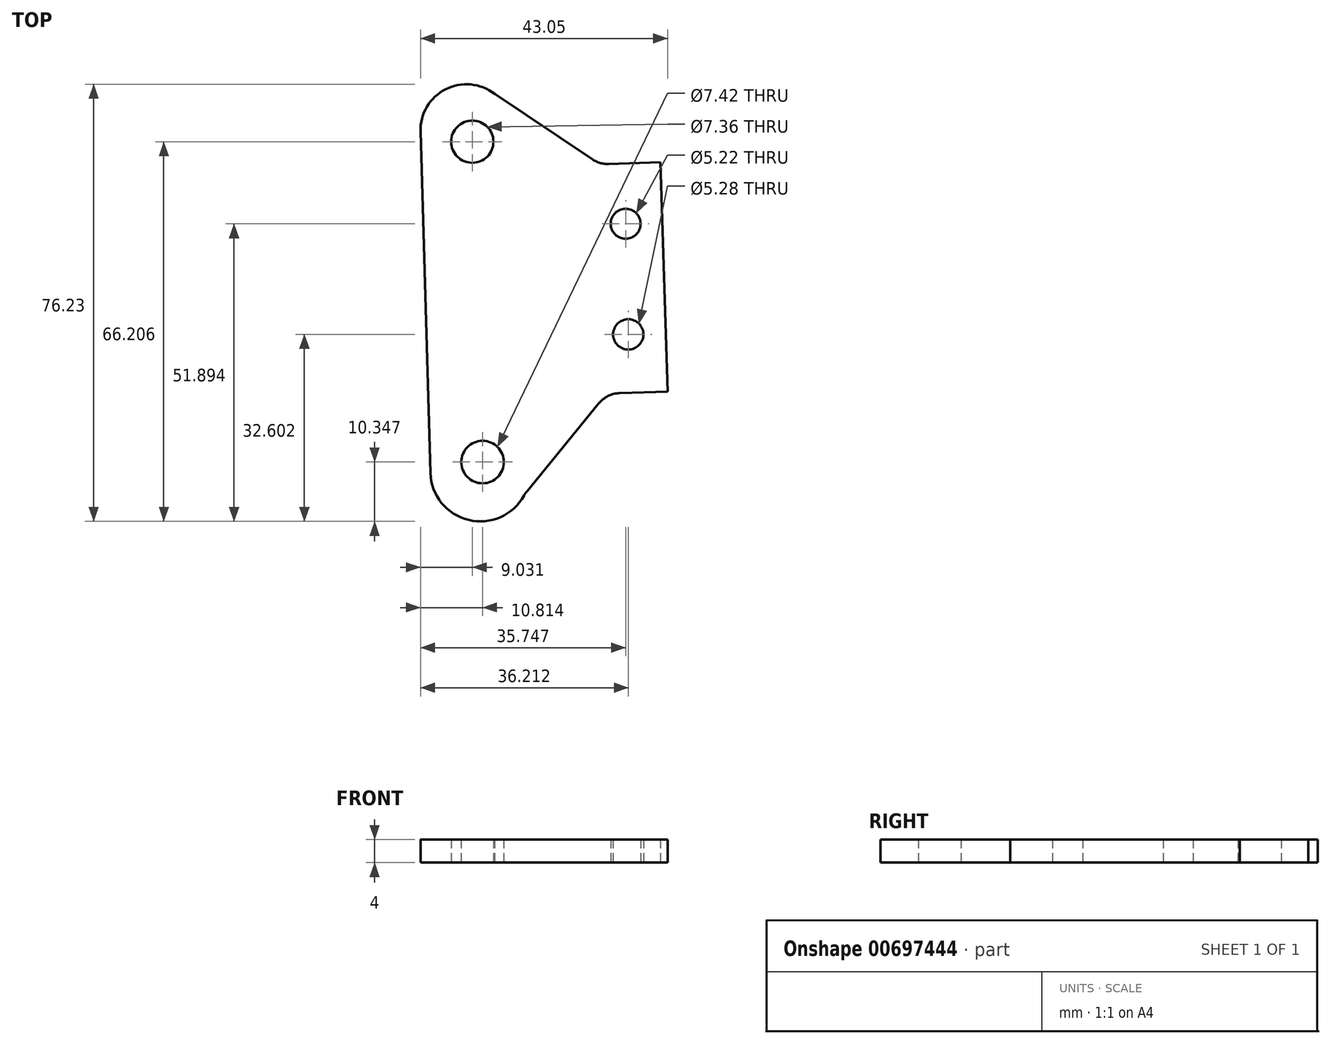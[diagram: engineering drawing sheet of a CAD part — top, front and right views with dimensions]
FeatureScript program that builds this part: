
annotation { "Feature Type Name" : "Feature", "Feature Type Description" : "" }
export const myFeature = defineFeature(function(context is Context, id is Id, definition is map)
    precondition{}
    {
        {
            var Q0;
            Q0=qCreatedBy(makeId("Top.planeOp"),FACE);
            var sketch = newSketch(context, id + "F0", { "sketchPlane" : qUnion([Q0])});
            skLineSegment(sketch, "E0", {"start": v(-13.1, -22.63) * mm, "end": v(-14.39, 17.35) * mm});
            skLineSegment(sketch, "E1", {"start": v(-13.1, -22.63) * mm, "end": v(-21.41, -22.9) * mm});
            skLineSegment(sketch, "E2", {"start": v(-14.39, 17.35) * mm, "end": v(-23.34, 17.06) * mm});
            skLineSegment(sketch, "E3", {"start": v(-56.15, 22.71) * mm, "end": v(-54.44, -36.82) * mm});
            skArc(sketch, "E4", {"start": v(-54.44, -36.82) * mm, "mid": v(-47.79, -45.02) * mm, "end": v(-38.12, -40.77) * mm});
            skArc(sketch, "E5", {"start": v(-43.27, 29.3) * mm, "mid": v(-51.8, 30.08) * mm, "end": v(-56.15, 22.71) * mm});
            skLineSegment(sketch, "E6", {"start": v(-43.27, 29.3) * mm, "end": v(-26.3, 17.9) * mm});
            skLineSegment(sketch, "E7", {"start": v(-37.62, -40.01) * mm, "end": v(-25.12, -24.73) * mm});
            skCircle(sketch, "E8", {"center": v(-45.35, -34.92) * mm, "radius": 3.7 * mm});
            skPoint(sketch, "E8.first.point", {"position": v(-49.01, -34.36) * mm});
            skPoint(sketch, "E8.second.point", {"position": v(-41.66, -35.31) * mm});
            skPoint(sketch, "E8.third.point", {"position": v(-44.89, -38.6) * mm});
            skCircle(sketch, "E9", {"center": v(-47.13, 20.94) * mm, "radius": 3.68 * mm});
            skPoint(sketch, "E9.first.point", {"position": v(-50.8, 21.12) * mm});
            skPoint(sketch, "E9.second.point", {"position": v(-43.45, 20.82) * mm});
            skPoint(sketch, "E9.third.point", {"position": v(-46.08, 17.4) * mm});
            skCircle(sketch, "E10", {"center": v(-20.41, 6.62) * mm, "radius": 2.6 * mm});
            skPoint(sketch, "E10.first.point", {"position": v(-23, 6.35) * mm});
            skPoint(sketch, "E10.second.point", {"position": v(-17.8, 6.47) * mm});
            skPoint(sketch, "E10.third.point", {"position": v(-20.26, 4.02) * mm});
            skCircle(sketch, "E11", {"center": v(-19.95, -12.67) * mm, "radius": 2.64 * mm});
            skPoint(sketch, "E11.first.point", {"position": v(-22.59, -12.72) * mm});
            skPoint(sketch, "E11.second.point", {"position": v(-17.33, -13.02) * mm});
            skPoint(sketch, "E11.third.point", {"position": v(-19.3, -15.23) * mm});
            skArc(sketch, "E12.filletArc", {"start": v(-21.41, -22.9) * mm, "mid": v(-23.47, -23.41) * mm, "end": v(-25.12, -24.73) * mm});
            skPoint(sketch, "E13.visualSharp", {"position": v(-37.94, -40.4) * mm});
            skArc(sketch, "E13.filletArc", {"start": v(-37.62, -40.01) * mm, "mid": v(-37.89, -40.38) * mm, "end": v(-38.12, -40.77) * mm});
            skArc(sketch, "E14.filletArc", {"start": v(-26.3, 17.9) * mm, "mid": v(-24.88, 17.25) * mm, "end": v(-23.34, 17.06) * mm});
            skSolve(sketch);
        }
        {
            var Q0;
            Q0 = qSketchRegion(id + "F0", true);
            extrude(context, id + "F1", {"entities" : qUnion([Q0]), "depth" : 4 * mm, "offsetDistance" : 25 * mm});
        }
    });
